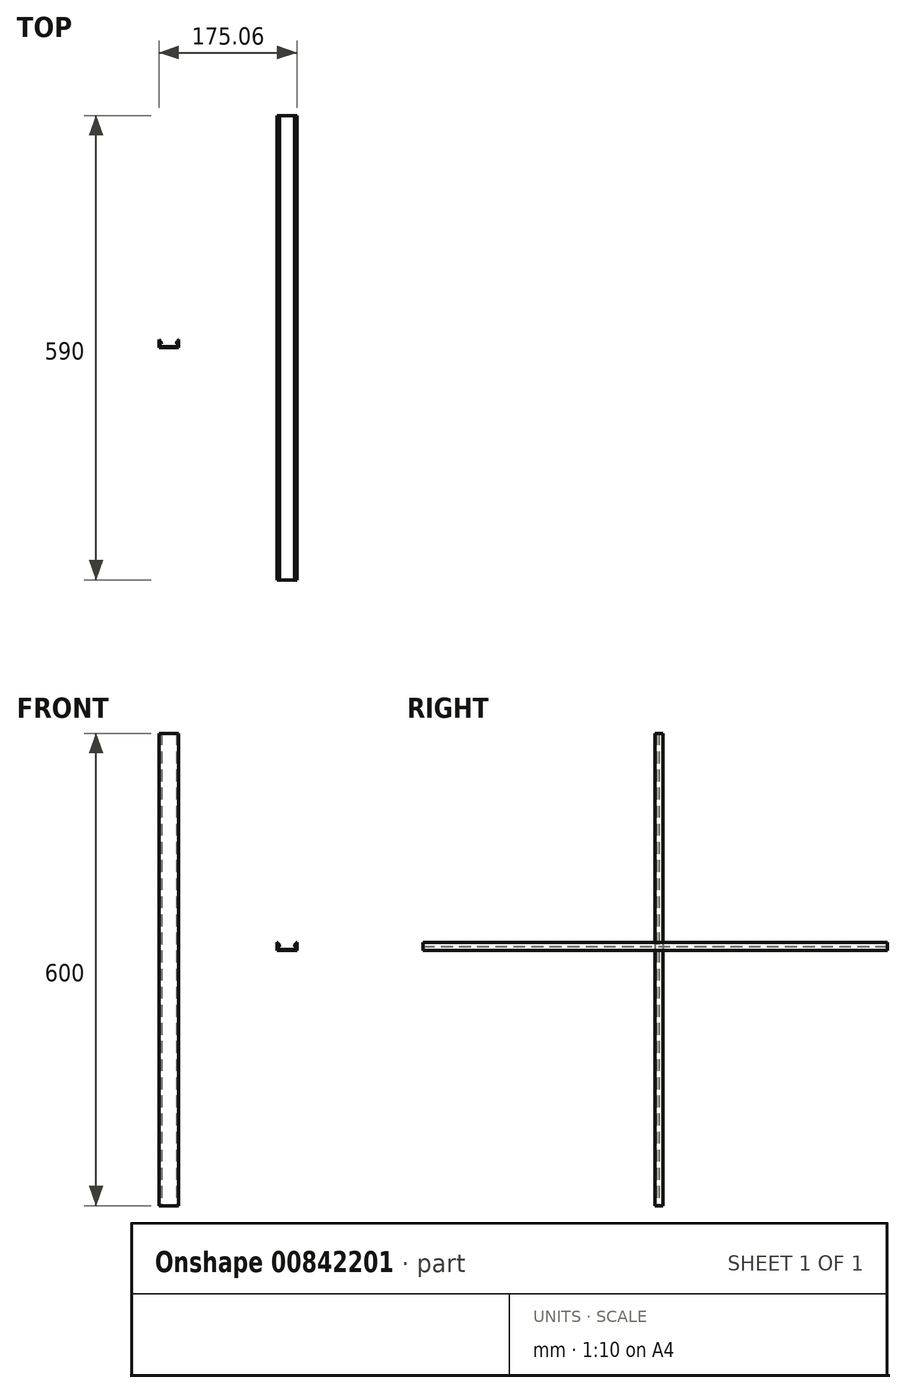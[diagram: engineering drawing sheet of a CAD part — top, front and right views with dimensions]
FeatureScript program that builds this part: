
annotation { "Feature Type Name" : "Feature", "Feature Type Description" : "" }
export const myFeature = defineFeature(function(context is Context, id is Id, definition is map)
    precondition{}
    {
        {
            var Q0;
            Q0=qCreatedBy(makeId("Top.planeOp"),FACE);
            var sketch = newSketch(context, id + "F0", { "sketchPlane" : qUnion([Q0])});
            skLineSegment(sketch, "E0", {"start": v(-95.87, 0) * mm, "end": v(-108.37, 0) * mm});
            skLineSegment(sketch, "E1", {"start": v(-108.37, 0) * mm, "end": v(-108.37, 9.5) * mm});
            skLineSegment(sketch, "E2.0", {"start": v(-106.87, 1.5) * mm, "end": v(-106.87, 5) * mm});
            skLineSegment(sketch, "E2.1", {"start": v(-95.87, 1.5) * mm, "end": v(-106.87, 1.5) * mm});
            skLineSegment(sketch, "E3", {"start": v(-106.87, 5) * mm, "end": v(-105.87, 5) * mm});
            skPoint(sketch, "E4.visualSharp", {"position": v(-105.37, 5) * mm});
            skPoint(sketch, "E5.start.orphan", {"position": v(-95.87, 0) * mm});
            skPoint(sketch, "E6.visualSharp", {"position": v(-108.37, 10) * mm});
            skLineSegment(sketch, "E7.MirrorCS", {"start": v(-95.87, 1.5) * mm, "end": v(-84.87, 1.5) * mm});
            skLineSegment(sketch, "E8.MirrorCS", {"start": v(-95.87, 0) * mm, "end": v(-83.37, 0) * mm});
            skLineSegment(sketch, "E9", {"start": v(-108.37, 9.5) * mm, "end": v(-108.37, 10) * mm});
            skLineSegment(sketch, "E10", {"start": v(-95.87, 1.5) * mm, "end": v(-95.87, 4.58) * mm});
            skLineSegment(sketch, "E11.MirrorCS", {"start": v(-84.87, 1.5) * mm, "end": v(-84.87, 5) * mm});
            skLineSegment(sketch, "E12.MirrorCS", {"start": v(-83.37, 0) * mm, "end": v(-83.37, 9.5) * mm});
            skLineSegment(sketch, "E13", {"start": v(-105.87, 5) * mm, "end": v(-105.37, 5) * mm});
            skArc(sketch, "E14", {"start": v(-105.37, 5) * mm, "mid": v(-106.22, 7.89) * mm, "end": v(-108.37, 10) * mm});
            skArc(sketch, "E15.MirrorCS", {"start": v(-86.37, 5) * mm, "mid": v(-85.52, 7.89) * mm, "end": v(-83.37, 10) * mm});
            skLineSegment(sketch, "E16.MirrorCS", {"start": v(-83.37, 9.5) * mm, "end": v(-83.37, 10) * mm});
            skLineSegment(sketch, "E17.MirrorCS", {"start": v(-85.87, 5) * mm, "end": v(-86.37, 5) * mm});
            skLineSegment(sketch, "E18.MirrorCS", {"start": v(-84.87, 5) * mm, "end": v(-85.87, 5) * mm});
            skSolve(sketch);
        }
        {
            var Q0;
            Q0=makeQuery(id+"F0.imprint","IMPRINT",FACE,{"disambiguationData":[TD([[makeQuery(id+"F0.imprint","IMPRINT",EDGE,{"derivedFrom":sQuery(id+"F0.wireOp",EDGE,"E0")}),-1.0]])]});
            extrude(context, id + "F1", {"entities" : qUnion([Q0]), "endBound" : BoundingType.SYMMETRIC, "depth" : 600 * mm, "offsetDistance" : 25 * mm});
        }
        {
            var Q0;
            Q0=qCreatedBy(makeId("Front.planeOp"),FACE);
            var sketch = newSketch(context, id + "F2", { "sketchPlane" : qUnion([Q0])});
            skLineSegment(sketch, "E19", {"start": v(54.2, 24.3) * mm, "end": v(41.7, 24.3) * mm});
            skLineSegment(sketch, "E20", {"start": v(41.7, 24.3) * mm, "end": v(41.7, 33.8) * mm});
            skLineSegment(sketch, "E21.0", {"start": v(43.2, 25.8) * mm, "end": v(43.2, 29.3) * mm});
            skLineSegment(sketch, "E21.1", {"start": v(54.2, 25.8) * mm, "end": v(43.2, 25.8) * mm});
            skLineSegment(sketch, "E22", {"start": v(43.2, 29.3) * mm, "end": v(44.2, 29.3) * mm});
            skPoint(sketch, "E23.visualSharp", {"position": v(44.7, 29.3) * mm});
            skPoint(sketch, "E24.start.orphan", {"position": v(54.2, 24.3) * mm});
            skPoint(sketch, "E25.visualSharp", {"position": v(41.7, 34.3) * mm});
            skLineSegment(sketch, "E26.MirrorCS", {"start": v(54.2, 25.8) * mm, "end": v(65.2, 25.8) * mm});
            skLineSegment(sketch, "E27.MirrorCS", {"start": v(54.2, 24.3) * mm, "end": v(66.7, 24.3) * mm});
            skLineSegment(sketch, "E28", {"start": v(41.7, 33.8) * mm, "end": v(41.7, 34.3) * mm});
            skLineSegment(sketch, "E29", {"start": v(54.2, 25.8) * mm, "end": v(54.2, 28.87) * mm});
            skLineSegment(sketch, "E30.MirrorCS", {"start": v(65.2, 25.8) * mm, "end": v(65.2, 29.3) * mm});
            skLineSegment(sketch, "E31.MirrorCS", {"start": v(66.7, 24.3) * mm, "end": v(66.7, 33.8) * mm});
            skLineSegment(sketch, "E32", {"start": v(44.2, 29.3) * mm, "end": v(44.7, 29.3) * mm});
            skArc(sketch, "E33", {"start": v(44.7, 29.3) * mm, "mid": v(43.84, 32.18) * mm, "end": v(41.7, 34.3) * mm});
            skArc(sketch, "E34.MirrorCS", {"start": v(63.7, 29.3) * mm, "mid": v(64.55, 32.18) * mm, "end": v(66.7, 34.3) * mm});
            skLineSegment(sketch, "E35.MirrorCS", {"start": v(66.7, 33.8) * mm, "end": v(66.7, 34.3) * mm});
            skLineSegment(sketch, "E36.MirrorCS", {"start": v(64.2, 29.3) * mm, "end": v(63.7, 29.3) * mm});
            skLineSegment(sketch, "E37.MirrorCS", {"start": v(65.2, 29.3) * mm, "end": v(64.2, 29.3) * mm});
            skSolve(sketch);
        }
        {
            var Q0;
            Q0=makeQuery(id+"F2.imprint","IMPRINT",FACE,{"disambiguationData":[TD([[makeQuery(id+"F2.imprint","IMPRINT",EDGE,{"derivedFrom":sQuery(id+"F2.wireOp",EDGE,"E19")}),-1.0]])]});
            extrude(context, id + "F3", {"entities" : qUnion([Q0]), "endBound" : BoundingType.SYMMETRIC, "depth" : 590 * mm, "offsetDistance" : 25 * mm});
        }
    });
